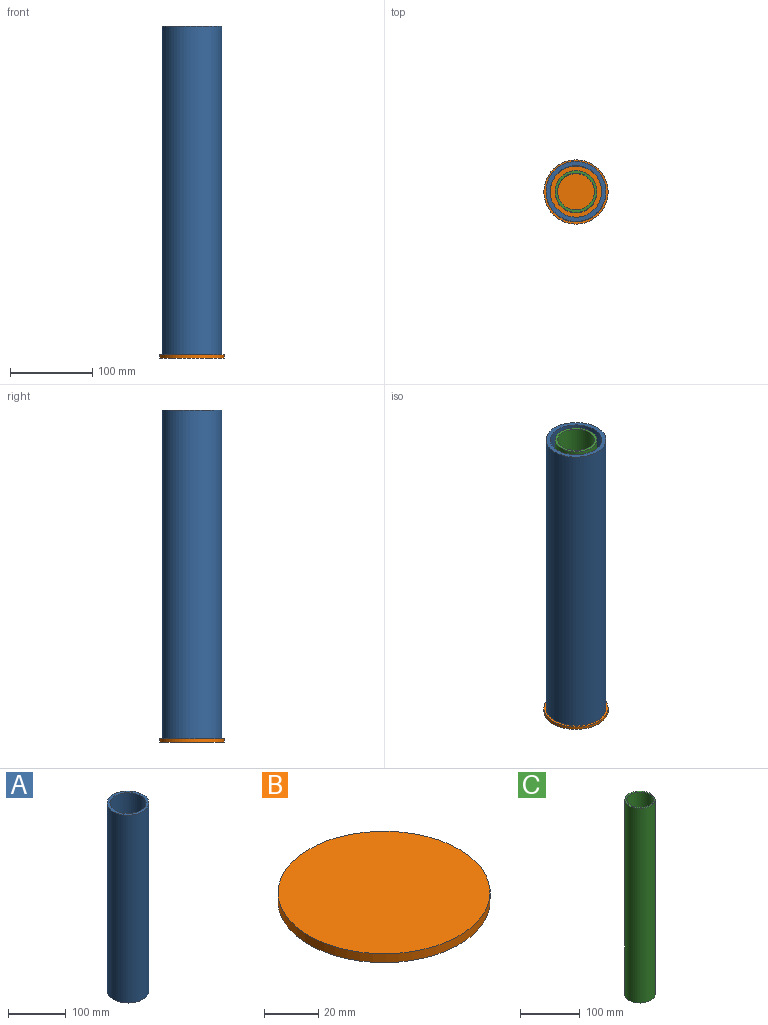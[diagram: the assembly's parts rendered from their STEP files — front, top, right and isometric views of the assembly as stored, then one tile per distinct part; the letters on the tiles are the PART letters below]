
ASSEMBLY  parts=3 mates=2
PART A: 4 faces, bbox 73x73x400 mm
  f0: cylinder r=36.52mm len=400mm, axis (0,0,-1), area 91772.2mm2, adj f1,f2
  f1: plane 73.03x73.03mm, normal (0,0,1), area 1100.2mm2, adj f0,f3
  f2: plane 73.03x73.03mm, normal (0,0,-1), area 1100.2mm2, adj f0,f3
  f3: cylinder r=31.36mm len=400mm, axis (0,0,-1), area 78803.7mm2, adj f1,f2
PART B: 3 faces, bbox 78.2x78.2x4 mm
  f0: cylinder r=39.09mm len=78.19mm, axis (0,0,-1), area 982.6mm2, adj f1,f2
  f1: plane 78.19x78.19mm, normal (0,0,1), area 4801.7mm2, adj f0
  f2: plane 78.19x78.19mm, normal (0,0,-1), area 4801.7mm2, adj f0
PART C: 4 faces, bbox 50.8x50.8x400 mm
  f0: cylinder r=25.4mm len=400mm, axis (0,0,-1), area 63837.2mm2, adj f1,f2
  f1: plane 50.8x50.8mm, normal (0,0,1), area 450.5mm2, adj f0,f3
  f2: plane 50.8x50.8mm, normal (0,0,-1), area 450.5mm2, adj f0,f3
  f3: cylinder r=22.4mm len=400mm, axis (0,0,-1), area 56297.3mm2, adj f1,f2
PLACE A t=(1.71,-0.12,0.33)mm
PLACE B t=(1.71,-0.12,-3.67)mm
PLACE C t=(1.71,-0.12,0.33)mm
MATE fastened C.f0 <-> B.f0  axis (0,0,-1) through (1.71,-0.12,0.33)mm
MATE fastened A.f0 <-> C.f0  axis (0,0,-1) through (1.71,-0.12,0.33)mm
